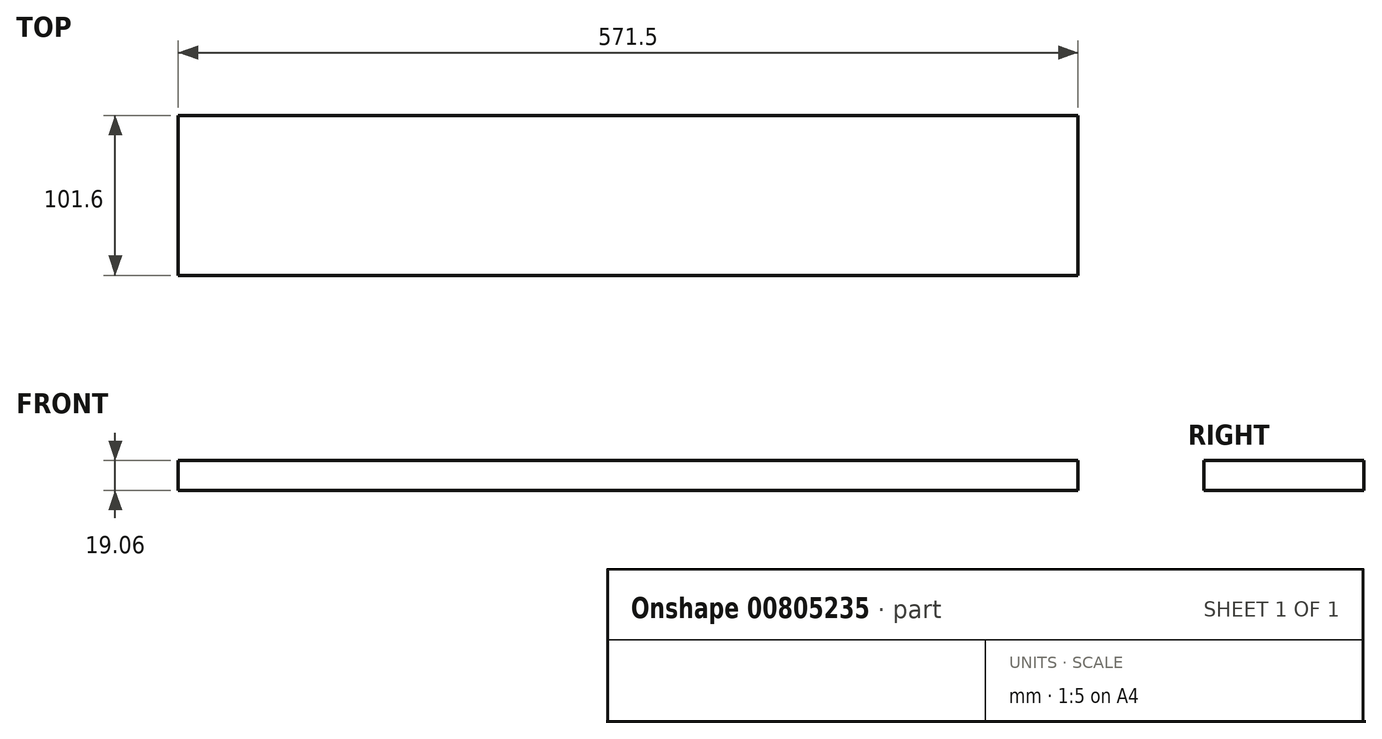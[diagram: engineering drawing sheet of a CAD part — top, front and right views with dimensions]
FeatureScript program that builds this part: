
annotation { "Feature Type Name" : "Feature", "Feature Type Description" : "" }
export const myFeature = defineFeature(function(context is Context, id is Id, definition is map)
    precondition{}
    {
        {
            var Q0;
            Q0=qCreatedBy(makeId("Top.planeOp"),FACE);
            var sketch = newSketch(context, id + "F0", { "sketchPlane" : qUnion([Q0])});
            skLineSegment(sketch, "E0.bottom", {"start": v(285.75, 50.8) * mm, "end": v(-285.75, 50.8) * mm});
            skLineSegment(sketch, "E0.top", {"start": v(285.75, -50.8) * mm, "end": v(-285.75, -50.8) * mm});
            skLineSegment(sketch, "E0.left", {"start": v(285.75, 50.8) * mm, "end": v(285.75, -50.8) * mm});
            skLineSegment(sketch, "E0.right", {"start": v(-285.75, 50.8) * mm, "end": v(-285.75, -50.8) * mm});
            skPoint(sketch, "E0.middle", {"position": v(0, 0) * mm});
            skSolve(sketch);
        }
        {
            var Q0;
            Q0=qSketchRegion(id+"F0",true);
            extrude(context, id + "F1", {"entities" : qUnion([Q0]), "endBound" : BoundingType.SYMMETRIC, "depth" : 19.05 * mm, "offsetDistance" : 25.4 * mm});
        }
    });
